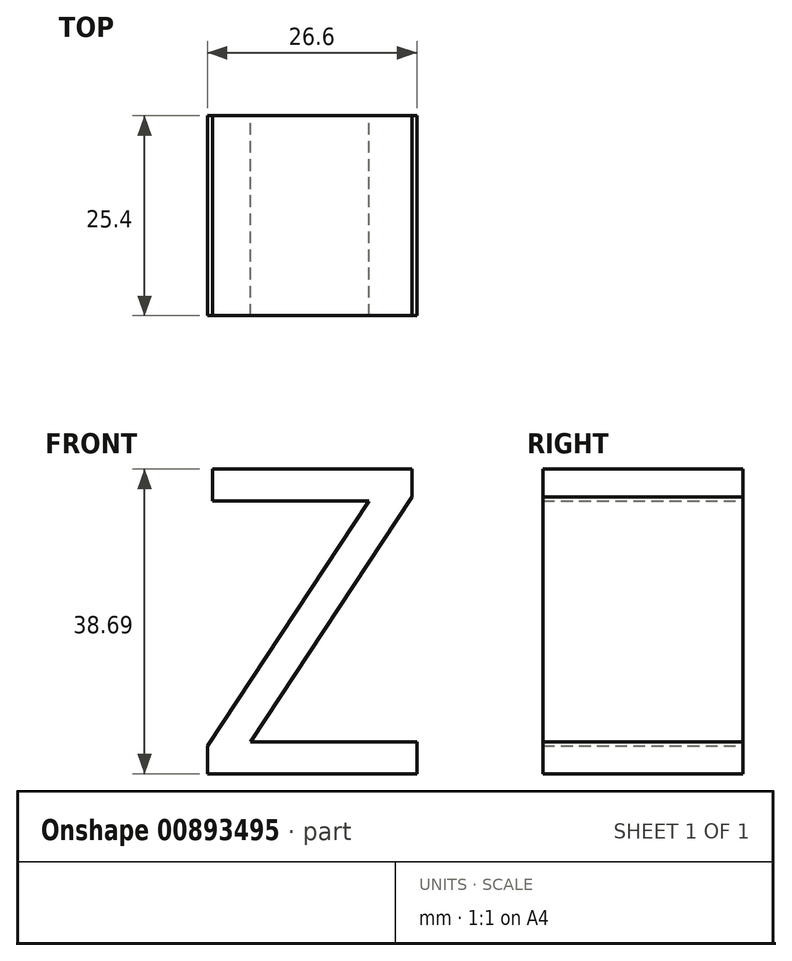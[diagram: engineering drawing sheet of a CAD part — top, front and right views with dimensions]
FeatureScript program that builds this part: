
annotation { "Feature Type Name" : "Feature", "Feature Type Description" : "" }
export const myFeature = defineFeature(function(context is Context, id is Id, definition is map)
    precondition{}
    {
        {
            var Q0;
            Q0=qCreatedBy(makeId("Front.planeOp"),FACE);
            var sketch = newSketch(context, id + "F0", { "sketchPlane" : qUnion([Q0])});
            skText(sketch, "E0", { "text": "Z\n", "fontName": "OpenSans-Regular.ttf"});
            const initialGuessF0  = {"E0": [-0.01755, -0.01681, 1, 0, 0.03902]};
            skSetInitialGuess(sketch, initialGuessF0);
            skSolve(sketch);
        }
        {
            var Q0;
            Q0 = qSketchRegion(id + "F0", true);
            extrude(context, id + "F1", {"entities" : qUnion([Q0]), "depth" : 25.4 * mm, "offsetDistance" : 25.4 * mm});
        }
    });
